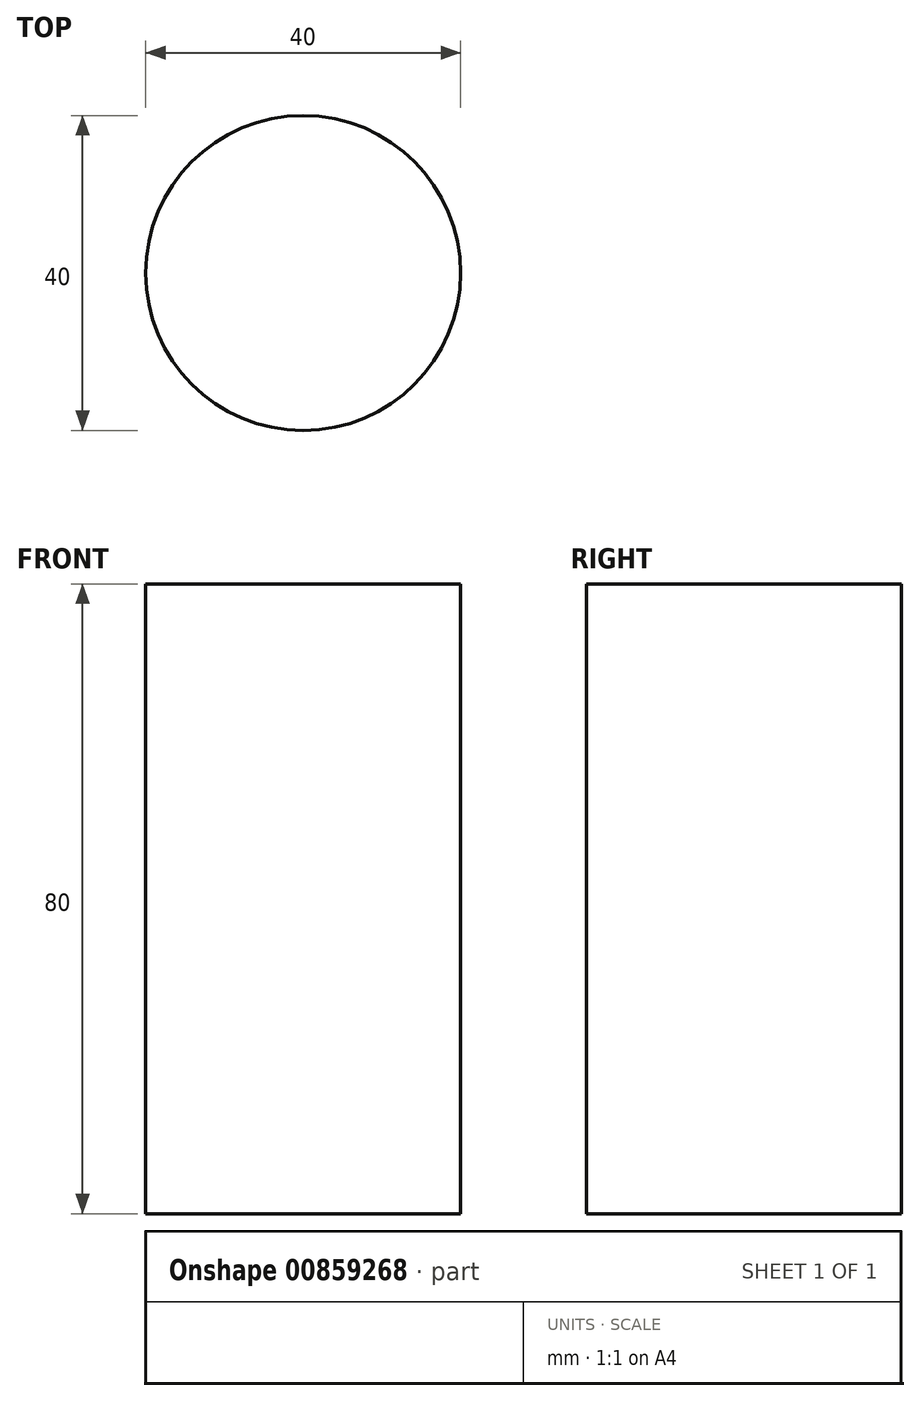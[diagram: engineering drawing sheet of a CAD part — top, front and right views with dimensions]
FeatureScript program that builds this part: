
annotation { "Feature Type Name" : "Feature", "Feature Type Description" : "" }
export const myFeature = defineFeature(function(context is Context, id is Id, definition is map)
    precondition{}
    {
        {
            var Q0;
            Q0=qCreatedBy(makeId("Front.planeOp"),FACE);
            var sketch = newSketch(context, id + "F0", { "sketchPlane" : qUnion([Q0])});
            skLineSegment(sketch, "E0", {"start": v(0, 0) * mm, "end": v(-20, 0) * mm});
            skLineSegment(sketch, "E1", {"start": v(-20, 0) * mm, "end": v(-20, 80) * mm});
            skLineSegment(sketch, "E2", {"start": v(-20, 80) * mm, "end": v(0, 80) * mm});
            skLineSegment(sketch, "E3", {"start": v(0, 80) * mm, "end": v(0, 0) * mm});
            skSolve(sketch);
        }
        {
            var Q0;
            Q0=makeQuery(id+"F0.imprint","IMPRINT",FACE,{"disambiguationData":[TD([[makeQuery(id+"F0.imprint","IMPRINT",EDGE,{"derivedFrom":sQuery(id+"F0.wireOp",EDGE,"E0")}),-1.0]])]});
            var Q1;
            Q1=sQuery(id+"F0.wireOp",EDGE,"E3");
            revolve(context, id + "F1", {"surfaceOperationType" : NewSurfaceOperationType.NEW, "entities" : qUnion([Q0]), "axis" : qUnion([Q1]), "revolveType" : RevolveType.FULL});
        }
    });
